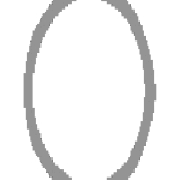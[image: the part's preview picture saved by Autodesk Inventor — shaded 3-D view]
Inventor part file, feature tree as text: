
AUTODESK INVENTOR PART (.ipt)
format: ipt  version: 2021 (Build 250183000, 183)  size: 109,568 bytes
history: native  units: in
note: dims shown in document units (in); Inventor stores cm internally (conversion verified against a paired STEP export)
features: other x4, sketch x3, plane x1
ambient origin geometry x8: Origin, YZ Plane, XZ Plane, XY Plane, X Axis, Y Axis, Z Axis, Center Point
bodies: Solid1 (feature_tree), Body (feature_tree)
feature tree (8):
  other  "Driven Length"
  other  "Frame Generator"
  other  "Start Plane"
  other  "End Plane"
  sketch  "Sketch"  dims[d2=31.4083in d4=-0.0in d5=31.4083in d6=0.12in d7=0.0in d8=90.0deg d9=31.4083in]
  sketch  "Sketch2"  dims[d0=1.0in]
  plane  "Work Plane3"
  sketch  "Sketch3"  dims[d1=0.065in]
